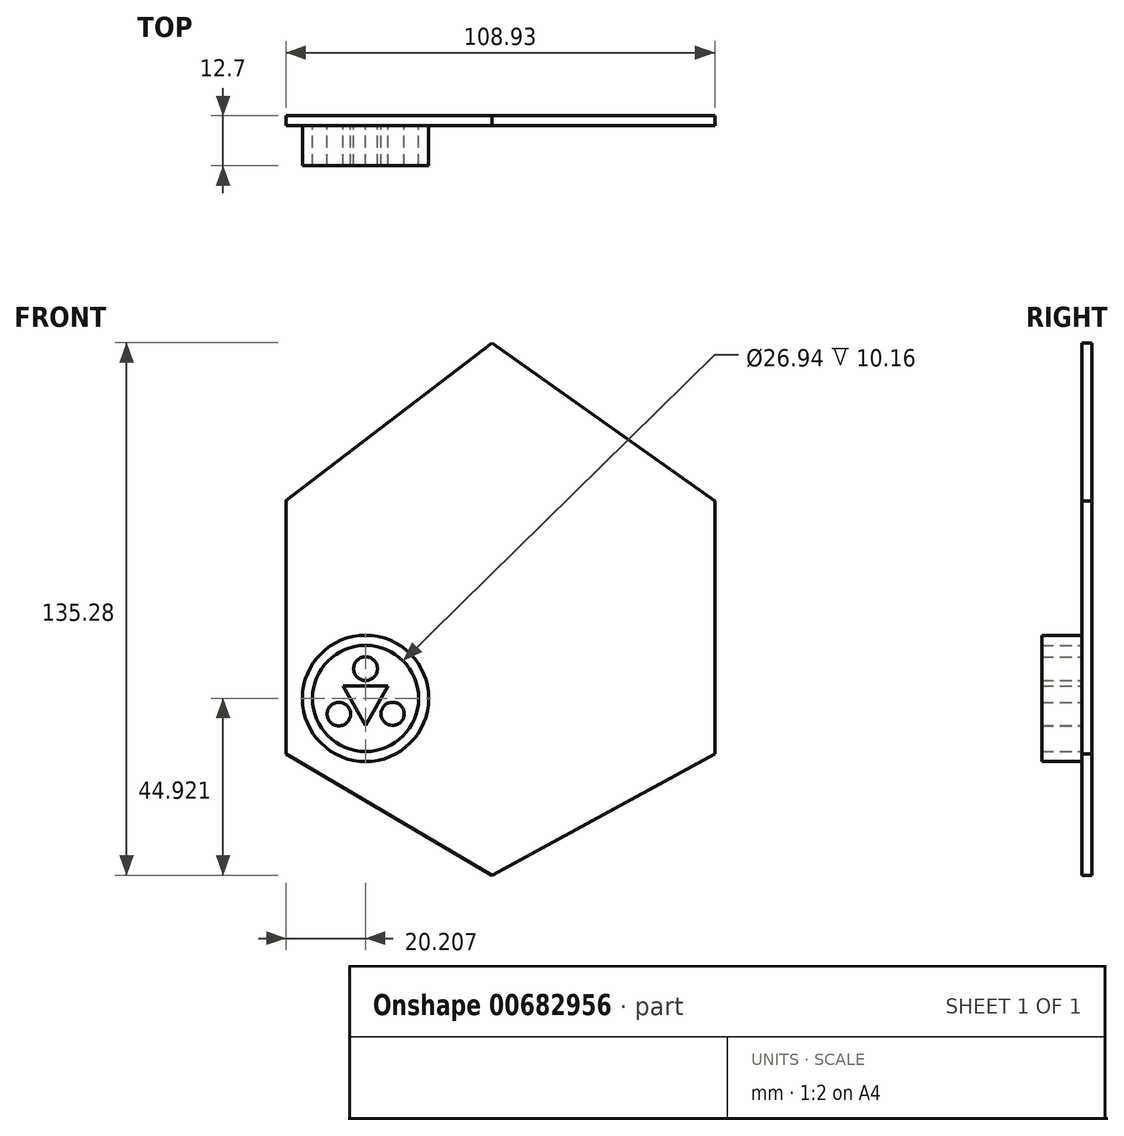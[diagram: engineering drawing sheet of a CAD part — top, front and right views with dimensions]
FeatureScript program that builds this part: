
annotation { "Feature Type Name" : "Feature", "Feature Type Description" : "" }
export const myFeature = defineFeature(function(context is Context, id is Id, definition is map)
    precondition{}
    {
        {
            var Q0;
            Q0=qCreatedBy(makeId("Front.planeOp"),FACE);
            var sketch = newSketch(context, id + "F0", { "sketchPlane" : qUnion([Q0])});
            skLineSegment(sketch, "E0", {"start": v(0, 68.56) * mm, "end": v(59.23, 26.56) * mm});
            skLineSegment(sketch, "E1", {"start": v(59.23, 26.56) * mm, "end": v(59.23, -40.56) * mm});
            skLineSegment(sketch, "E2", {"start": v(59.23, -40.56) * mm, "end": v(0, -72.79) * mm});
            skLineSegment(sketch, "E3", {"start": v(0, -72.79) * mm, "end": v(-54.78, -40.56) * mm});
            skLineSegment(sketch, "E4", {"start": v(-54.78, -40.56) * mm, "end": v(-54.78, 26.56) * mm});
            skLineSegment(sketch, "E5", {"start": v(-54.78, 26.56) * mm, "end": v(0, 68.56) * mm});
            skSolve(sketch);
        }
        {
            var Q0;
            Q0=makeQuery(id+"F0.imprint","IMPRINT",FACE,{"disambiguationData":[TD([[makeQuery(id+"F0.imprint","IMPRINT",EDGE,{"derivedFrom":sQuery(id+"F0.wireOp",EDGE,"E0")}),-1.0]])]});
            extrude(context, id + "F1", {"entities" : qUnion([Q0]), "depth" : 12.7 * mm, "offsetDistance" : 25.4 * mm});
        }
        {
            var Q0;
            Q0=makeQuery(id+"F1.opExtrude","CAP_FACE",FACE,{"disambiguationData":[OSD([sQuery(id+"F0.wireOp",EDGE,"E0"),sQuery(id+"F0.wireOp",EDGE,"E1"),sQuery(id+"F0.wireOp",EDGE,"E2"),sQuery(id+"F0.wireOp",EDGE,"E3"),sQuery(id+"F0.wireOp",EDGE,"E4"),sQuery(id+"F0.wireOp",EDGE,"E5")])],"isStart":false});
            extrude(context, id + "F2", {"entities" : qUnion([Q0]), "operationType" : NewBodyOperationType.REMOVE, "oppositeDirection" : true, "depth" : 2.54 * mm, "offsetDistance" : 25.4 * mm});
        }
        {
            var Q0;
            Q0=makeQuery(id+"F2.boolean.opBoolean","COPY",FACE,{"derivedFrom":makeQuery(id+"F2.opExtrude","CAP_FACE",FACE,{"disambiguationData":[OSD([sQuery(id+"F0.wireOp",EDGE,"E0"),sQuery(id+"F0.wireOp",EDGE,"E1"),sQuery(id+"F0.wireOp",EDGE,"E2"),sQuery(id+"F0.wireOp",EDGE,"E3"),sQuery(id+"F0.wireOp",EDGE,"E4"),sQuery(id+"F0.wireOp",EDGE,"E5")])],"isStart":false})});
            extrude(context, id + "F3", {"entities" : qUnion([Q0]), "operationType" : NewBodyOperationType.REMOVE, "oppositeDirection" : true, "depth" : 7.62 * mm, "offsetDistance" : 25.4 * mm});
        }
        {
            var Q0;
            Q0=makeQuery(id+"F1.opExtrude","SWEPT_FACE",FACE,{"disambiguationData":[OSD([sQuery(id+"F0.wireOp",EDGE,"E0")])]});
            extrude(context, id + "F4", {"entities" : qUnion([Q0]), "operationType" : NewBodyOperationType.REMOVE, "oppositeDirection" : true, "depth" : 2.54 * mm, "offsetDistance" : 25.4 * mm});
        }
        {
            var Q0;
            Q0=makeQuery(id+"F1.opExtrude","SWEPT_FACE",FACE,{"disambiguationData":[OSD([sQuery(id+"F0.wireOp",EDGE,"E5")])]});
            extrude(context, id + "F5", {"entities" : qUnion([Q0]), "operationType" : NewBodyOperationType.REMOVE, "oppositeDirection" : true, "depth" : 2.54 * mm, "offsetDistance" : 25.4 * mm});
        }
        {
            var Q0;
            Q0=makeQuery(id+"F1.opExtrude","SWEPT_FACE",FACE,{"disambiguationData":[OSD([sQuery(id+"F0.wireOp",EDGE,"E1")])]});
            extrude(context, id + "F6", {"entities" : qUnion([Q0]), "operationType" : NewBodyOperationType.REMOVE, "oppositeDirection" : true, "depth" : 2.54 * mm, "offsetDistance" : 25.4 * mm});
        }
        {
            var Q0;
            Q0=makeQuery(id+"F1.opExtrude","SWEPT_FACE",FACE,{"disambiguationData":[OSD([sQuery(id+"F0.wireOp",EDGE,"E4")])]});
            extrude(context, id + "F7", {"entities" : qUnion([Q0]), "operationType" : NewBodyOperationType.REMOVE, "oppositeDirection" : true, "depth" : 2.54 * mm, "offsetDistance" : 25.4 * mm});
        }
        {
            var Q0;
            Q0=makeQuery(id+"F1.opExtrude","SWEPT_FACE",FACE,{"disambiguationData":[OSD([sQuery(id+"F0.wireOp",EDGE,"E3")])]});
            extrude(context, id + "F8", {"entities" : qUnion([Q0]), "operationType" : NewBodyOperationType.REMOVE, "oppositeDirection" : true, "depth" : 2.54 * mm, "offsetDistance" : 25.4 * mm});
        }
        {
            var Q0;
            Q0=makeQuery(id+"F1.opExtrude","SWEPT_FACE",FACE,{"disambiguationData":[OSD([sQuery(id+"F0.wireOp",EDGE,"E2")])]});
            extrude(context, id + "F9", {"entities" : qUnion([Q0]), "operationType" : NewBodyOperationType.REMOVE, "oppositeDirection" : true, "depth" : 2.54 * mm, "offsetDistance" : 25.4 * mm});
        }
        {
            var Q0;
            Q0=makeQuery(id+"F3.boolean.opBoolean","COPY",FACE,{"derivedFrom":makeQuery(id+"F3.opExtrude","CAP_FACE",FACE,{"disambiguationData":[OSD([sQuery(id+"F0.wireOp",EDGE,"E0"),sQuery(id+"F0.wireOp",EDGE,"E1"),sQuery(id+"F0.wireOp",EDGE,"E2"),sQuery(id+"F0.wireOp",EDGE,"E3"),sQuery(id+"F0.wireOp",EDGE,"E4"),sQuery(id+"F0.wireOp",EDGE,"E5")])],"isStart":false})});
            var sketch = newSketch(context, id + "F10", { "sketchPlane" : qUnion([Q0])});
            skCircle(sketch, "E6", {"center": v(-32.03, -24.95) * mm, "radius": 16.05 * mm});
            skCircle(sketch, "E7", {"center": v(-32.03, -24.95) * mm, "radius": 13.47 * mm});
            skCircle(sketch, "E8", {"center": v(-32.03, -17.38) * mm, "radius": 3.02 * mm});
            skCircle(sketch, "E9", {"center": v(-38.81, -28.92) * mm, "radius": 2.99 * mm});
            skCircle(sketch, "E10", {"center": v(-25.15, -28.86) * mm, "radius": 2.95 * mm});
            skLineSegment(sketch, "E11", {"start": v(-37.73, -21.83) * mm, "end": v(-26.3, -21.83) * mm});
            skLineSegment(sketch, "E12", {"start": v(-26.3, -21.83) * mm, "end": v(-31.97, -31.76) * mm});
            skLineSegment(sketch, "E13", {"start": v(-31.97, -31.76) * mm, "end": v(-37.73, -21.83) * mm});
            skSolve(sketch);
        }
        {
            var Q0;
            Q0=makeQuery(id+"F10.imprint","IMPRINT",FACE,{"disambiguationData":[TD([[makeQuery(id+"F10.imprint","IMPRINT",EDGE,{"derivedFrom":sQuery(id+"F10.wireOp",EDGE,"E6")}),1.0]])]});
            var Q1;
            Q1=makeQuery(id+"F10.imprint","IMPRINT",FACE,{"disambiguationData":[TD([[makeQuery(id+"F10.imprint","IMPRINT",EDGE,{"derivedFrom":sQuery(id+"F10.wireOp",EDGE,"E8")}),1.0]])]});
            var Q2;
            Q2=makeQuery(id+"F10.imprint","IMPRINT",FACE,{"disambiguationData":[TD([[makeQuery(id+"F10.imprint","IMPRINT",EDGE,{"derivedFrom":sQuery(id+"F10.wireOp",EDGE,"E10")}),1.0]])]});
            var Q3;
            Q3=makeQuery(id+"F10.imprint","IMPRINT",FACE,{"disambiguationData":[TD([[makeQuery(id+"F10.imprint","IMPRINT",EDGE,{"derivedFrom":sQuery(id+"F10.wireOp",EDGE,"E9")}),1.0]])]});
            var Q4;
            Q4=makeQuery(id+"F10.imprint","IMPRINT",FACE,{"disambiguationData":[TD([[makeQuery(id+"F10.imprint","IMPRINT",EDGE,{"derivedFrom":sQuery(id+"F10.wireOp",EDGE,"E11")}),-1.0]])]});
            extrude(context, id + "F11", {"entities" : qUnion([Q0, Q1, Q2, Q3, Q4]), "operationType" : NewBodyOperationType.ADD, "depth" : 10.16 * mm, "offsetDistance" : 25.4 * mm});
        }
    });
